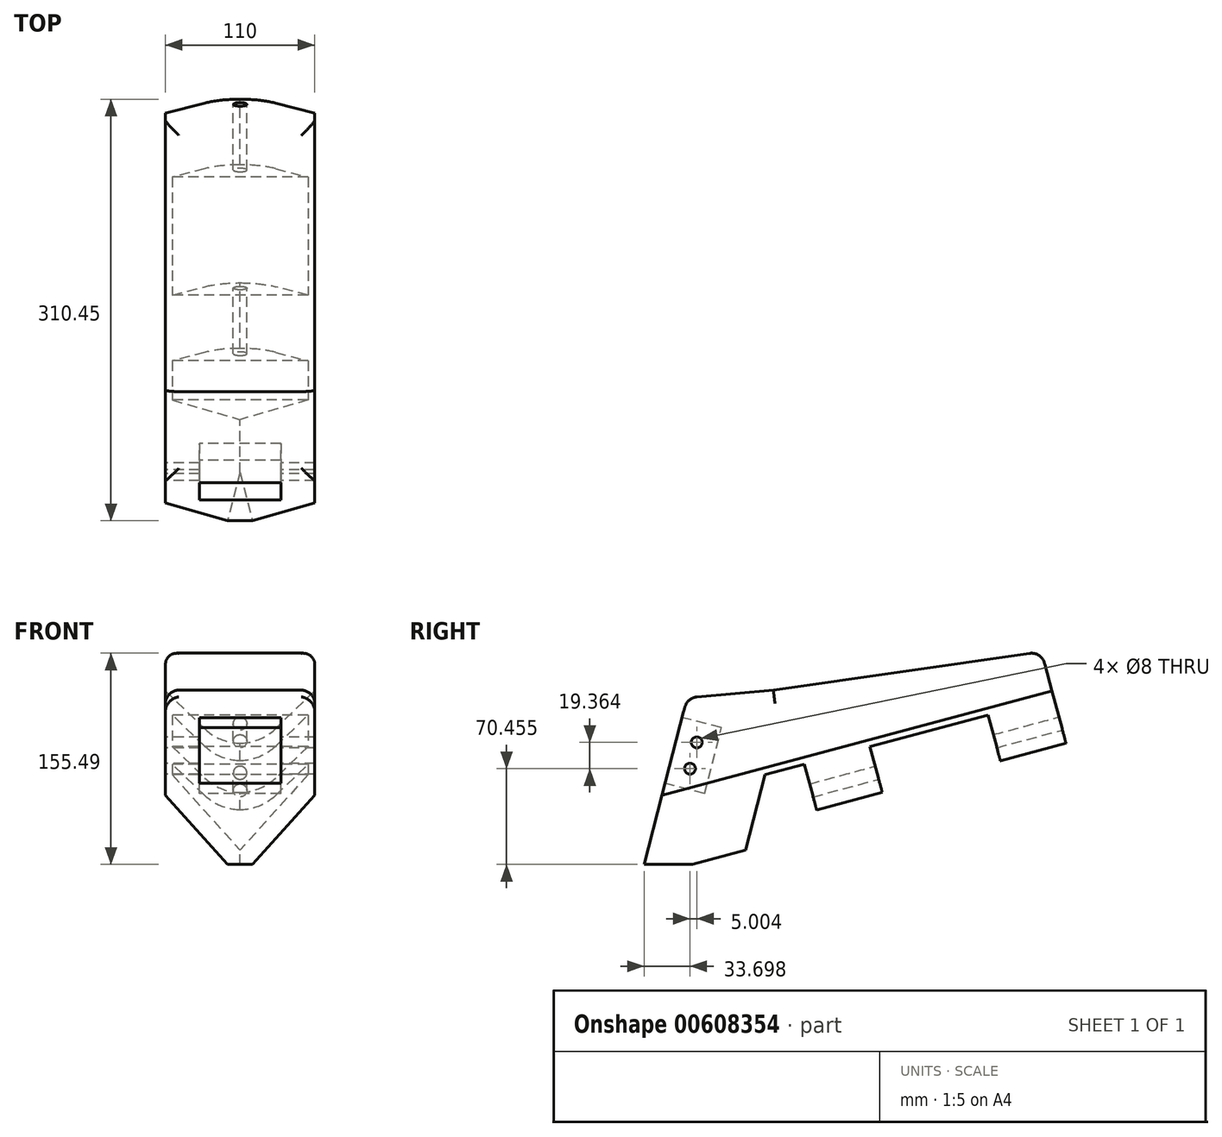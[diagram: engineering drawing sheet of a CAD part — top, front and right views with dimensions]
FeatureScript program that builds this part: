
annotation { "Feature Type Name" : "Feature", "Feature Type Description" : "" }
export const myFeature = defineFeature(function(context is Context, id is Id, definition is map)
    precondition{}
    {
        {
            var Q0;
            Q0=qCreatedBy(makeId("Right.planeOp"),FACE);
            var sketch = newSketch(context, id + "F0", { "sketchPlane" : qUnion([Q0])});
            skLineSegment(sketch, "E0", {"start": v(-188.45, -110.86) * mm, "end": v(-156.76, 11.76) * mm});
            skLineSegment(sketch, "E1", {"start": v(-116.63, -110.86) * mm, "end": v(-188.45, -110.86) * mm});
            skLineSegment(sketch, "E2", {"start": v(-160.52, -2.76) * mm, "end": v(-131.47, -10.27) * mm});
            skLineSegment(sketch, "E3", {"start": v(-131.47, -10.27) * mm, "end": v(-143.98, -58.68) * mm});
            skLineSegment(sketch, "E4", {"start": v(-143.98, -58.68) * mm, "end": v(-173.03, -51.17) * mm});
            skLineSegment(sketch, "E5", {"start": v(-146, -6.52) * mm, "end": v(-158.5, -54.93) * mm, "construction": true});
            skCircle(sketch, "E6", {"center": v(-149.75, -21.04) * mm, "radius": 4 * mm});
            skCircle(sketch, "E7", {"center": v(-154.75, -40.4) * mm, "radius": 4 * mm});
            skLineSegment(sketch, "E8", {"start": v(-70.58, -37.06) * mm, "end": v(-61.52, -70.86) * mm});
            skLineSegment(sketch, "E9", {"start": v(-13.23, -57.92) * mm, "end": v(-22.28, -24.12) * mm});
            skLineSegment(sketch, "E10", {"start": v(-22.28, -24.12) * mm, "end": v(64.65, -0.82) * mm});
            skLineSegment(sketch, "E11", {"start": v(64.65, -0.82) * mm, "end": v(73.7, -34.63) * mm});
            skLineSegment(sketch, "E12", {"start": v(122, -21.69) * mm, "end": v(103.92, 45.79) * mm});
            skLineSegment(sketch, "E13", {"start": v(-61.52, -70.86) * mm, "end": v(-13.23, -57.92) * mm});
            skLineSegment(sketch, "E14.trimOffspring", {"start": v(73.7, -34.63) * mm, "end": v(122, -21.69) * mm});
            skLineSegment(sketch, "E15", {"start": v(-156.76, 11.76) * mm, "end": v(-93.33, 17.41) * mm});
            skLineSegment(sketch, "E16", {"start": v(-93.33, 17.41) * mm, "end": v(103.92, 45.79) * mm});
            skLineSegment(sketch, "E17", {"start": v(-61.52, -70.86) * mm, "end": v(122, -21.69) * mm, "construction": true});
            skLineSegment(sketch, "E18", {"start": v(-70.58, -37.06) * mm, "end": v(112.94, 12.12) * mm, "construction": true});
            skLineSegment(sketch, "E19", {"start": v(-70.58, -37.06) * mm, "end": v(-99.56, -44.82) * mm});
            skLineSegment(sketch, "E20", {"start": v(-99.56, -44.82) * mm, "end": v(-116.63, -110.86) * mm});
            skSolve(sketch);
        }
        {
            var Q0;
            {var subQ1=sQuery(id+"F0.wireOp",EDGE,"E1");Q0=makeQuery(id+"F0.imprint","IMPRINT",FACE,{"disambiguationData":[TD([[makeQuery(id+"F0.imprint","IMPRINT",EDGE,{"derivedFrom":subQ1}),-1.0]])]});}
            var Q1;
            {var subQ0=sQuery(id+"F0.wireOp",EDGE,"E2");Q1=makeQuery(id+"F0.imprint","IMPRINT",FACE,{"disambiguationData":[TD([[makeQuery(id+"F0.imprint","IMPRINT",EDGE,{"derivedFrom":subQ0}),-1.0]])]});}
            extrude(context, id + "F1", {"entities" : qUnion([Q0, Q1]), "endBound" : BoundingType.SYMMETRIC, "depth" : 110 * mm, "offsetDistance" : 25 * mm});
        }
        {
            var Q0;
            Q0=makeQuery(id+"F1.opExtrude","SWEPT_FACE",FACE,{"disambiguationData":[OSD([sQuery(id+"F0.wireOp",EDGE,"E0")])]});
            var sketch = newSketch(context, id + "F2", { "sketchPlane" : qUnion([Q0])});
            skLineSegment(sketch, "E21.bottom", {"start": v(30, -92.84) * mm, "end": v(-30, -92.84) * mm});
            skLineSegment(sketch, "E21.top", {"start": v(30, -42.84) * mm, "end": v(-30, -42.84) * mm});
            skLineSegment(sketch, "E21.left", {"start": v(30, -92.84) * mm, "end": v(30, -42.84) * mm});
            skLineSegment(sketch, "E21.right", {"start": v(-30, -92.84) * mm, "end": v(-30, -42.84) * mm});
            skPoint(sketch, "E21.middle", {"position": v(0, -67.84) * mm});
            skSolve(sketch);
        }
        {
            var Q0;
            Q0=makeQuery(id+"F2.imprint","IMPRINT",FACE,{"disambiguationData":[TD([[makeQuery(id+"F2.imprint","IMPRINT",EDGE,{"derivedFrom":sQuery(id+"F2.wireOp",EDGE,"E21.bottom")}),-1.0]])]});
            extrude(context, id + "F3", {"entities" : qUnion([Q0]), "operationType" : NewBodyOperationType.REMOVE, "oppositeDirection" : true, "depth" : 30 * mm, "offsetDistance" : 25 * mm});
        }
        {
            var Q0;
            Q0=makeQuery(id+"F1.opExtrude","SWEPT_FACE",FACE,{"disambiguationData":[OSD([sQuery(id+"F0.wireOp",EDGE,"E12")])]});
            var sketch = newSketch(context, id + "F4", { "sketchPlane" : qUnion([Q0])});
            skCircle(sketch, "E22", {"center": v(0, -37.53) * mm, "radius": 5 * mm});
            skSolve(sketch);
        }
        {
            var Q0;
            Q0=sQuery(id+"F4.wireOp",VERTEX,"E22.center");
            var Q1;
            Q1=makeQuery(id+"F1.opExtrude","SWEPT_BODY",BODY,{"disambiguationData":[OSD([sQuery(id+"F0.wireOp",EDGE,"E0"),sQuery(id+"F0.wireOp",EDGE,"E1"),sQuery(id+"F0.wireOp",EDGE,"E6"),sQuery(id+"F0.wireOp",EDGE,"E7"),sQuery(id+"F0.wireOp",EDGE,"E8"),sQuery(id+"F0.wireOp",EDGE,"E9"),sQuery(id+"F0.wireOp",EDGE,"E10"),sQuery(id+"F0.wireOp",EDGE,"E11"),sQuery(id+"F0.wireOp",EDGE,"E12"),sQuery(id+"F0.wireOp",EDGE,"E13"),sQuery(id+"F0.wireOp",EDGE,"E14.trimOffspring"),sQuery(id+"F0.wireOp",EDGE,"E15"),sQuery(id+"F0.wireOp",EDGE,"E16"),sQuery(id+"F0.wireOp",EDGE,"E19"),sQuery(id+"F0.wireOp",EDGE,"E20")])]});
            hole(context, id + "F5", {"style" : HoleStyle.SIMPLE, "endStyle" : HoleEndStyle.BLIND, "holeDiameter" : 10 * mm, "majorDiameter" : 5 * mm, "holeDepth" : 190 * mm, "isTappedThrough" : true, "tappedDepth" : 12 * mm, "tapClearance" : 3, "locations" : qUnion([Q0]), "scope" : qUnion([Q1])});
        }
        {
            var Q0;
            Q0=makeQuery(id+"F1.opExtrude","CAP_EDGE",EDGE,{"disambiguationData":[OSD([sQuery(id+"F0.wireOp",EDGE,"E13")])],"isStart":false});
            var Q1;
            Q1=makeQuery(id+"F1.opExtrude","CAP_EDGE",EDGE,{"disambiguationData":[OSD([sQuery(id+"F0.wireOp",EDGE,"E14.trimOffspring")])],"isStart":false});
            var Q2;
            Q2=makeQuery(id+"F1.opExtrude","CAP_EDGE",EDGE,{"disambiguationData":[OSD([sQuery(id+"F0.wireOp",EDGE,"E13")])],"isStart":true});
            var Q3;
            Q3=makeQuery(id+"F1.opExtrude","CAP_EDGE",EDGE,{"disambiguationData":[OSD([sQuery(id+"F0.wireOp",EDGE,"E14.trimOffspring")])],"isStart":true});
            chamfer(context, id + "F6", {"entities" : qUnion([Q0, Q1, Q2, Q3]), "width" : 40 * mm, "tangentPropagation" : true});
        }
        {
            var Q0;
            Q0=makeQuery(id+"F1.opExtrude","CAP_EDGE",EDGE,{"disambiguationData":[OSD([sQuery(id+"F0.wireOp",EDGE,"E15")])],"isStart":false});
            var Q1;
            Q1=makeQuery(id+"F1.opExtrude","SWEPT_EDGE",EDGE,{"disambiguationData":[OSD([sQuery(id+"F0.wireOp",EDGE,"E0"),sQuery(id+"F0.wireOp",EDGE,"E15")])]});
            var Q2;
            Q2=makeQuery(id+"F1.opExtrude","CAP_EDGE",EDGE,{"disambiguationData":[OSD([sQuery(id+"F0.wireOp",EDGE,"E15")])],"isStart":true});
            var Q3;
            Q3=makeQuery(id+"F1.opExtrude","CAP_EDGE",EDGE,{"disambiguationData":[OSD([sQuery(id+"F0.wireOp",EDGE,"E16")])],"isStart":false});
            var Q4;
            Q4=makeQuery(id+"F1.opExtrude","CAP_EDGE",EDGE,{"disambiguationData":[OSD([sQuery(id+"F0.wireOp",EDGE,"E16")])],"isStart":true});
            var Q5;
            Q5=makeQuery(id+"F1.opExtrude","SWEPT_EDGE",EDGE,{"disambiguationData":[OSD([sQuery(id+"F0.wireOp",EDGE,"E12"),sQuery(id+"F0.wireOp",EDGE,"E16")])]});
            fillet(context, id + "F7", {"entities" : qUnion([Q0, Q1, Q2, Q3, Q4, Q5]), "radius" : 10 * mm, "tangentPropagation" : true, "allowEdgeOverflow" : false});
        }
        {
            var Q0;
            {var subQ0=sQuery(id+"F0.wireOp",EDGE,"E14.trimOffspring");Q0=makeQuery(id+"F6.opChamfer","BLEND_EDGE",EDGE,{"blendedFrom":[makeQuery(id+"F1.opExtrude","CAP_EDGE",EDGE,{"disambiguationData":[OSD([subQ0])],"isStart":false}),makeQuery(id+"F1.opExtrude","SWEPT_FACE",FACE,{"disambiguationData":[OSD([subQ0])]})],"blendedInto":[makeQuery(id+"F1.opExtrude","SWEPT_FACE",FACE,{"disambiguationData":[OSD([subQ0])]})]});}
            var Q1;
            Q1=makeQuery(id+"F6.opChamfer","BLEND_EDGE",EDGE,{"blendedFrom":[makeQuery(id+"F1.opExtrude","CAP_EDGE",EDGE,{"disambiguationData":[OSD([sQuery(id+"F0.wireOp",EDGE,"E13")])],"isStart":true}),makeQuery(id+"F1.opExtrude","SWEPT_FACE",FACE,{"disambiguationData":[OSD([sQuery(id+"F0.wireOp",EDGE,"E14.trimOffspring")])]})],"blendedInto":[makeQuery(id+"F1.opExtrude","SWEPT_FACE",FACE,{"disambiguationData":[OSD([sQuery(id+"F0.wireOp",EDGE,"E14.trimOffspring")])]})]});
            var Q2;
            Q2=makeQuery(id+"F6.opChamfer","BLEND_EDGE",EDGE,{"blendedFrom":[makeQuery(id+"F1.opExtrude","CAP_EDGE",EDGE,{"disambiguationData":[OSD([sQuery(id+"F0.wireOp",EDGE,"E14.trimOffspring")])],"isStart":false}),makeQuery(id+"F1.opExtrude","SWEPT_FACE",FACE,{"disambiguationData":[OSD([sQuery(id+"F0.wireOp",EDGE,"E13")])]})],"blendedInto":[makeQuery(id+"F1.opExtrude","SWEPT_FACE",FACE,{"disambiguationData":[OSD([sQuery(id+"F0.wireOp",EDGE,"E13")])]})]});
            var Q3;
            {var subQ0=sQuery(id+"F0.wireOp",EDGE,"E13");Q3=makeQuery(id+"F6.opChamfer","BLEND_EDGE",EDGE,{"blendedFrom":[makeQuery(id+"F1.opExtrude","CAP_EDGE",EDGE,{"disambiguationData":[OSD([subQ0])],"isStart":true}),makeQuery(id+"F1.opExtrude","SWEPT_FACE",FACE,{"disambiguationData":[OSD([subQ0])]})],"blendedInto":[makeQuery(id+"F1.opExtrude","SWEPT_FACE",FACE,{"disambiguationData":[OSD([subQ0])]})]});}
            fillet(context, id + "F8", {"entities" : qUnion([Q0, Q1, Q2, Q3]), "radius" : 38 * mm, "tangentPropagation" : true, "allowEdgeOverflow" : false});
        }
    });
